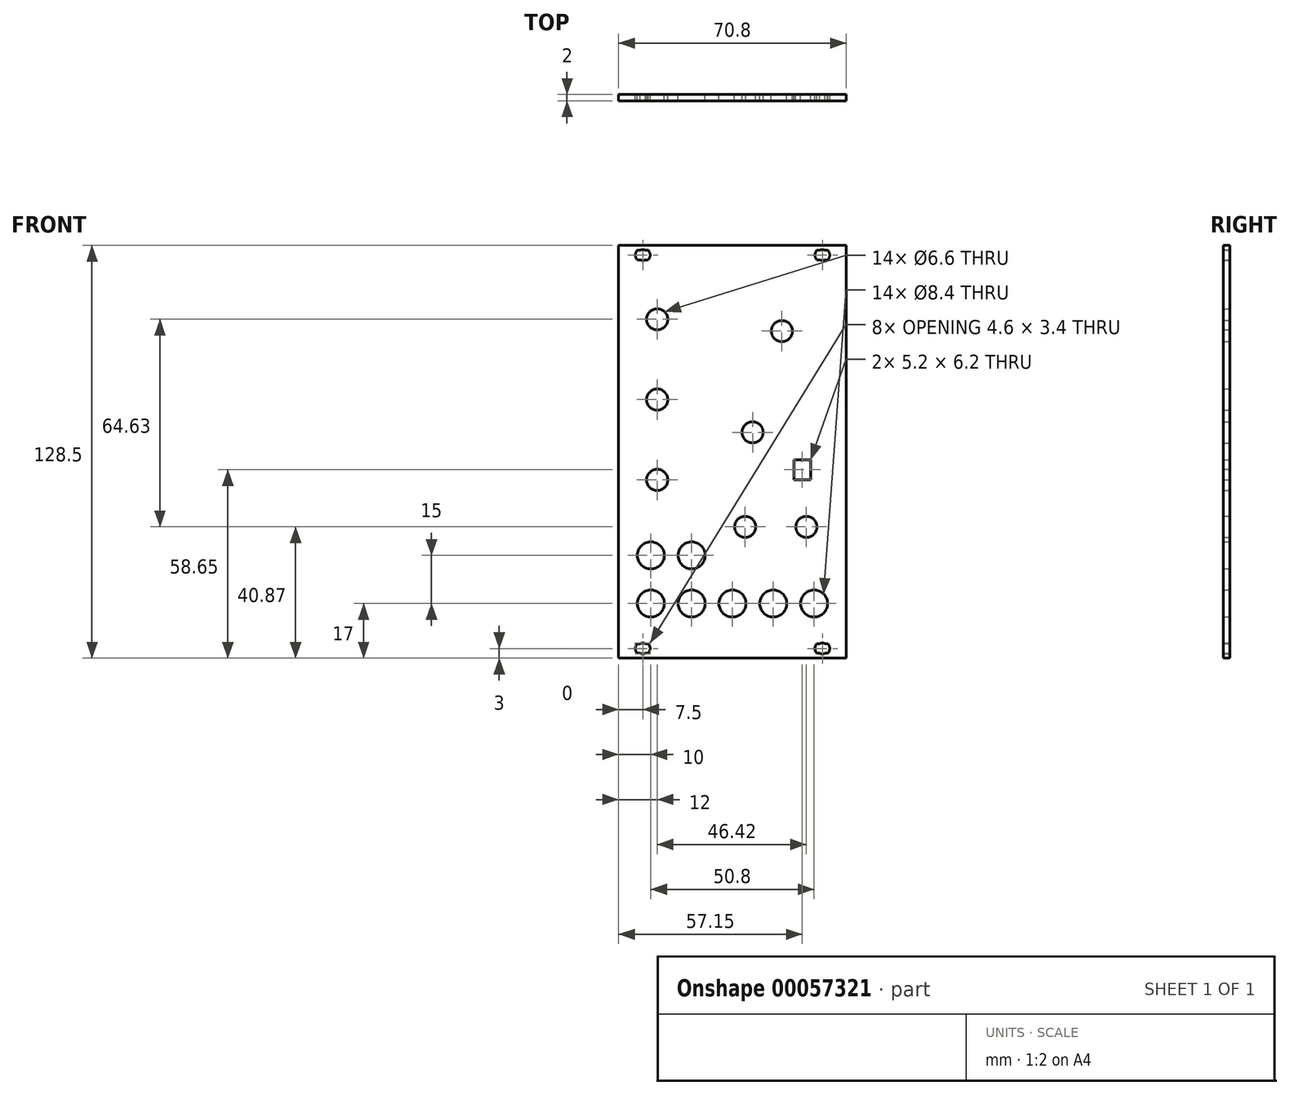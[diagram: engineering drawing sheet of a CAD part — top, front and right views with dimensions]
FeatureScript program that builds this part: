
annotation { "Feature Type Name" : "Feature", "Feature Type Description" : "" }
export const myFeature = defineFeature(function(context is Context, id is Id, definition is map)
    precondition{}
    {
        {
            var Q0;
            Q0=qCreatedBy(makeId("Front.planeOp"),FACE);
            var sketch = newSketch(context, id + "F0", { "sketchPlane" : qUnion([Q0])});
            skLineSegment(sketch, "E0", {"start": v(28.78, -59.75) * mm, "end": v(29.68, -59.75) * mm});
            skLineSegment(sketch, "E1", {"start": v(26.28, -59.75) * mm, "end": v(27.18, -59.75) * mm});
            skLineSegment(sketch, "E2", {"start": v(28.78, -62.75) * mm, "end": v(29.68, -62.75) * mm});
            skLineSegment(sketch, "E3", {"start": v(26.28, -62.75) * mm, "end": v(27.18, -62.75) * mm});
            skLineSegment(sketch, "E4", {"start": v(-29.6, 59.75) * mm, "end": v(-28.7, 59.75) * mm});
            skLineSegment(sketch, "E5", {"start": v(-27.1, 59.75) * mm, "end": v(-26.2, 59.75) * mm});
            skLineSegment(sketch, "E6", {"start": v(-29.6, 62.75) * mm, "end": v(-28.7, 62.75) * mm});
            skLineSegment(sketch, "E7", {"start": v(-27.1, 62.75) * mm, "end": v(-26.2, 62.75) * mm});
            skLineSegment(sketch, "E8", {"start": v(26.28, 59.75) * mm, "end": v(27.18, 59.75) * mm});
            skLineSegment(sketch, "E9", {"start": v(28.78, 59.75) * mm, "end": v(29.68, 59.75) * mm});
            skLineSegment(sketch, "E10", {"start": v(26.28, 62.75) * mm, "end": v(27.18, 62.75) * mm});
            skLineSegment(sketch, "E11", {"start": v(28.78, 62.75) * mm, "end": v(29.68, 62.75) * mm});
            skLineSegment(sketch, "E12", {"start": v(-29.6, -62.75) * mm, "end": v(-28.7, -62.75) * mm});
            skLineSegment(sketch, "E13", {"start": v(-27.1, -62.75) * mm, "end": v(-26.2, -62.75) * mm});
            skLineSegment(sketch, "E14", {"start": v(-29.6, -59.75) * mm, "end": v(-28.7, -59.75) * mm});
            skLineSegment(sketch, "E15", {"start": v(-27.1, -59.75) * mm, "end": v(-26.2, -59.75) * mm});
            skLineSegment(sketch, "E16", {"start": v(-35.4, -64.25) * mm, "end": v(-35.4, 64.25) * mm});
            skLineSegment(sketch, "E17", {"start": v(-35.4, 64.25) * mm, "end": v(15.1, 64.25) * mm});
            skLineSegment(sketch, "E18", {"start": v(-35.4, -64.25) * mm, "end": v(-35.4, -61.25) * mm});
            skLineSegment(sketch, "E19", {"start": v(-35.4, 64.25) * mm, "end": v(25.2, 64.25) * mm});
            skLineSegment(sketch, "E20", {"start": v(-35.4, 64.25) * mm, "end": v(35.4, 64.25) * mm});
            skLineSegment(sketch, "E21", {"start": v(35.4, -64.25) * mm, "end": v(35.4, 64.25) * mm});
            skLineSegment(sketch, "E22", {"start": v(-35.4, -64.25) * mm, "end": v(35.4, -64.25) * mm});
            skArc(sketch, "E23", {"start": v(26.28, -59.75) * mm, "mid": v(25.68, -61.25) * mm, "end": v(26.28, -62.75) * mm});
            skArc(sketch, "E24", {"start": v(29.68, -62.75) * mm, "mid": v(30.28, -61.25) * mm, "end": v(29.68, -59.75) * mm});
            skArc(sketch, "E25", {"start": v(28.78, -59.75) * mm, "mid": v(27.98, -59.55) * mm, "end": v(27.18, -59.75) * mm});
            skArc(sketch, "E26", {"start": v(27.18, -62.75) * mm, "mid": v(27.98, -62.95) * mm, "end": v(28.78, -62.75) * mm});
            skArc(sketch, "E27", {"start": v(-28.7, 59.75) * mm, "mid": v(-27.9, 59.55) * mm, "end": v(-27.1, 59.75) * mm});
            skArc(sketch, "E28", {"start": v(-27.1, 62.75) * mm, "mid": v(-27.9, 62.95) * mm, "end": v(-28.7, 62.75) * mm});
            skArc(sketch, "E29", {"start": v(-26.2, 59.75) * mm, "mid": v(-25.6, 61.25) * mm, "end": v(-26.2, 62.75) * mm});
            skArc(sketch, "E30", {"start": v(-29.6, 62.75) * mm, "mid": v(-30.2, 61.25) * mm, "end": v(-29.6, 59.75) * mm});
            skArc(sketch, "E31", {"start": v(27.18, 59.75) * mm, "mid": v(27.98, 59.55) * mm, "end": v(28.78, 59.75) * mm});
            skArc(sketch, "E32", {"start": v(28.78, 62.75) * mm, "mid": v(27.98, 62.95) * mm, "end": v(27.18, 62.75) * mm});
            skArc(sketch, "E33", {"start": v(29.68, 59.75) * mm, "mid": v(30.28, 61.25) * mm, "end": v(29.68, 62.75) * mm});
            skArc(sketch, "E34", {"start": v(26.28, 62.75) * mm, "mid": v(25.68, 61.25) * mm, "end": v(26.28, 59.75) * mm});
            skArc(sketch, "E35", {"start": v(-28.7, -62.75) * mm, "mid": v(-27.9, -62.95) * mm, "end": v(-27.1, -62.75) * mm});
            skArc(sketch, "E36", {"start": v(-27.1, -59.75) * mm, "mid": v(-27.9, -59.55) * mm, "end": v(-28.7, -59.75) * mm});
            skArc(sketch, "E37", {"start": v(-26.2, -62.75) * mm, "mid": v(-25.6, -61.25) * mm, "end": v(-26.2, -59.75) * mm});
            skArc(sketch, "E38", {"start": v(-29.6, -59.75) * mm, "mid": v(-30.2, -61.25) * mm, "end": v(-29.6, -62.75) * mm});
            skCircle(sketch, "E39", {"center": v(12.7, -47.25) * mm, "radius": 4.2 * mm});
            skCircle(sketch, "E40", {"center": v(-25.4, -32.25) * mm, "radius": 4.2 * mm});
            skCircle(sketch, "E41", {"center": v(-12.7, -32.25) * mm, "radius": 4.2 * mm});
            skCircle(sketch, "E42", {"center": v(-25.4, -47.25) * mm, "radius": 4.2 * mm});
            skCircle(sketch, "E43", {"center": v(-12.7, -47.25) * mm, "radius": 4.2 * mm});
            skCircle(sketch, "E44", {"center": v(0, -47.25) * mm, "radius": 4.2 * mm});
            skCircle(sketch, "E45", {"center": v(25.4, -47.25) * mm, "radius": 4.2 * mm});
            skCircle(sketch, "E46", {"center": v(15.4, 37.58) * mm, "radius": 3.3 * mm});
            skCircle(sketch, "E47", {"center": v(3.97, -23.38) * mm, "radius": 3.3 * mm});
            skCircle(sketch, "E48", {"center": v(23.02, -23.38) * mm, "radius": 3.3 * mm});
            skCircle(sketch, "E49", {"center": v(6.27, 6.05) * mm, "radius": 3.3 * mm});
            skCircle(sketch, "E50", {"center": v(-23.4, 41.25) * mm, "radius": 3.3 * mm});
            skCircle(sketch, "E51", {"center": v(-23.4, 16.25) * mm, "radius": 3.3 * mm});
            skCircle(sketch, "E52", {"center": v(-23.4, -8.75) * mm, "radius": 3.3 * mm});
            skLineSegment(sketch, "E53", {"start": v(19.15, -8.7) * mm, "end": v(19.15, -2.5) * mm});
            skLineSegment(sketch, "E54", {"start": v(19.15, -2.5) * mm, "end": v(24.35, -2.5) * mm});
            skLineSegment(sketch, "E55", {"start": v(19.15, -8.7) * mm, "end": v(24.35, -8.7) * mm});
            skLineSegment(sketch, "E56", {"start": v(24.35, -8.7) * mm, "end": v(24.35, -2.5) * mm});
            skSolve(sketch);
        }
        {
            var Q0;
            Q0 = qSketchRegion(id + "F0", true);
            extrude(context, id + "F1", {"entities" : qUnion([Q0]), "depth" : 2 * mm});
        }
    });
